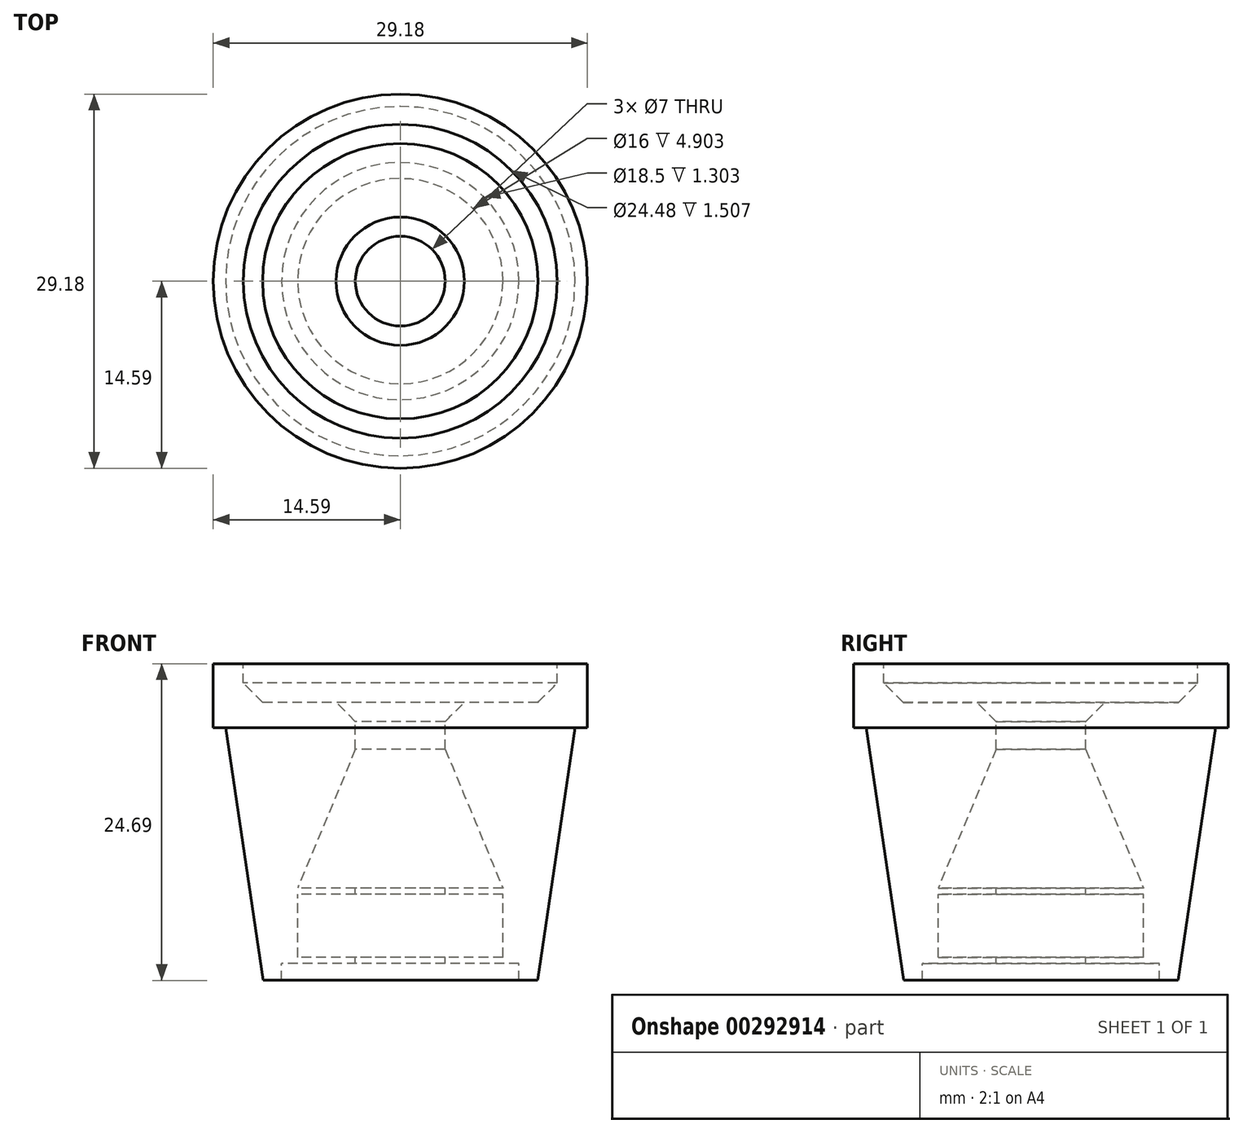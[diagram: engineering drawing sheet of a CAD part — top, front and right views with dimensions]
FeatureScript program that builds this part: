
annotation { "Feature Type Name" : "Feature", "Feature Type Description" : "" }
export const myFeature = defineFeature(function(context is Context, id is Id, definition is map)
    precondition{}
    {
        {
            var Q0;
            Q0=qCreatedBy(makeId("Front.planeOp"),FACE);
            var sketch = newSketch(context, id + "F0", { "sketchPlane" : qUnion([Q0])});
            skLineSegment(sketch, "E0", {"start": v(3.5, 27.28) * mm, "end": v(12.24, 27.28) * mm});
            skLineSegment(sketch, "E1", {"start": v(12.24, 27.28) * mm, "end": v(12.24, 30.28) * mm});
            skLineSegment(sketch, "E2", {"start": v(12.24, 30.28) * mm, "end": v(14.6, 30.28) * mm});
            skLineSegment(sketch, "E3", {"start": v(14.6, 30.28) * mm, "end": v(14.6, 25.28) * mm});
            skLineSegment(sketch, "E4", {"start": v(14.6, 25.28) * mm, "end": v(13.62, 25.28) * mm});
            skLineSegment(sketch, "E5", {"start": v(13.62, 25.28) * mm, "end": v(10.7, 5.6) * mm});
            skLineSegment(sketch, "E6", {"start": v(10.7, 5.6) * mm, "end": v(9.25, 5.6) * mm});
            skLineSegment(sketch, "E7", {"start": v(9.25, 5.6) * mm, "end": v(9.25, 6.9) * mm});
            skLineSegment(sketch, "E8", {"start": v(9.25, 6.9) * mm, "end": v(3.5, 6.9) * mm});
            skLineSegment(sketch, "E9", {"start": v(3.5, 6.9) * mm, "end": v(3.5, 7.4) * mm});
            skLineSegment(sketch, "E10", {"start": v(3.5, 7.4) * mm, "end": v(8, 7.4) * mm});
            skLineSegment(sketch, "E11", {"start": v(8, 7.4) * mm, "end": v(8, 12.3) * mm});
            skLineSegment(sketch, "E12", {"start": v(8, 12.3) * mm, "end": v(3.5, 12.3) * mm});
            skLineSegment(sketch, "E13", {"start": v(3.5, 12.3) * mm, "end": v(3.5, 12.8) * mm});
            skLineSegment(sketch, "E14", {"start": v(3.5, 12.8) * mm, "end": v(8, 12.8) * mm});
            skLineSegment(sketch, "E15", {"start": v(8, 12.8) * mm, "end": v(3.5, 23.6) * mm});
            skLineSegment(sketch, "E16", {"start": v(3.5, 23.6) * mm, "end": v(3.5, 27.28) * mm});
            skLineSegment(sketch, "E17", {"start": v(0, 36.22) * mm, "end": v(0, -4.19) * mm, "construction": true});
            skSolve(sketch);
        }
        {
            var Q0;
            Q0 = qSketchRegion(id + "F0", true);
            var Q1;
            Q1=sQuery(id+"F0.wireOp",EDGE,"E17");
            revolve(context, id + "F1", {"entities" : qUnion([Q0]), "axis" : qUnion([Q1]), "revolveType" : RevolveType.FULL});
        }
        {
            var Q0;
            Q0=makeQuery(id+"F1.opRevolve","SWEPT_EDGE",EDGE,{"disambiguationData":[OSD([sQuery(id+"F0.wireOp",EDGE,"E0"),sQuery(id+"F0.wireOp",EDGE,"E16")])]});
            var Q1;
            Q1=makeQuery(id+"F1.opRevolve","SWEPT_EDGE",EDGE,{"disambiguationData":[OSD([sQuery(id+"F0.wireOp",EDGE,"E0"),sQuery(id+"F0.wireOp",EDGE,"E1")])]});
            chamfer(context, id + "F2", {"entities" : qUnion([Q0, Q1]), "width" : 1.5 * mm, "tangentPropagation" : true});
        }
    });
